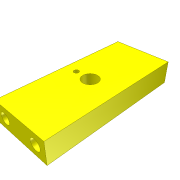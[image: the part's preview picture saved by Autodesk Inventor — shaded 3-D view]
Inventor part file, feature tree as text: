
AUTODESK INVENTOR PART (.ipt)
format: ipt  version: unknown  size: 187,392 bytes
history: native  units: in
note: dims shown in document units (in); Inventor stores cm internally (conversion verified against a paired STEP export)
features: extrude x2, sketch x2
ambient origin geometry x8: Origin, YZ Plane, XZ Plane, XY Plane, X Axis, Y Axis, Z Axis, Center Point
feature tree (4):
  extrude  "Extrusion43"  Depth=0.1303in
  extrude  "Extrusion44"  Depth=0.0787in
  sketch  "Sketch43"  dims[d200=0.0787in d201=0.1303in]
  sketch  "Sketch44"  dims[d202=0.1303in d203=0.0787in d204=0.0787in d205=0.0787in d206=0.1575in d207=0.9843in d208=0.0in d209=0.1181in d211=0.0394in d212=0.3937in d213=0.0in d214=0.1181in]
